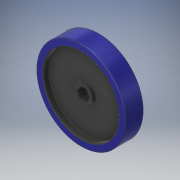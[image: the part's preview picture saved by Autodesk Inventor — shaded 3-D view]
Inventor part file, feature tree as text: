
AUTODESK INVENTOR PART (.ipt)
format: ipt  version: 2017 (Build 210142000, 142)  size: 197,120 bytes
history: native  units: in
note: dims shown in document units (in); Inventor stores cm internally (conversion verified against a paired STEP export)
features: extrude x4, sketch x4, fillet x1, projected_geometry x1
ambient origin geometry x8: Origin, YZ Plane, XZ Plane, XY Plane, X Axis, Y Axis, Z Axis, Center Point
bodies: Solid1 (feature_tree)
feature tree (10):
  extrude  "Extrusion1"  Depth=0.3in TaperAngle=0.0deg
  extrude  "Extrusion2"  Depth=0.8in TaperAngle=0.0deg
  extrude  "Extrusion3"  Depth=0.6in TaperAngle=0.0deg
  extrude  "Extrusion4"  Depth=0.6in TaperAngle=0.0deg
  fillet  "Fillet1"  Radius=0.03in
  sketch  "Sketch1"  dims[d0=3.875in d1=0.3in d2=0.0in]
  sketch  "Sketch2"  dims[d3=3.275in d4=0.8in d5=0.0in]
  projected_geometry  "Projected Loop1"
  sketch  "Sketch3"  dims[d6=0.8in d7=0.6in d8=0.0in]
  sketch  "Sketch4"  dims[d9=0.5in d10=0.6in d11=0.0in d12=0.03in]
